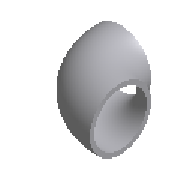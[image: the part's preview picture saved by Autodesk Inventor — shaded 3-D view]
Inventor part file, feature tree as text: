
AUTODESK INVENTOR PART (.ipt)
format: ipt  version: 2023.2 (Build 272271030, 271C)  size: 188,928 bytes
history: native  units: mm (DEFAULTED — no unit token found)
features: other x4, sketch x2, sweep x1
ambient origin geometry x8: Origin, YZ Plane, XZ Plane, XY Plane, X Axis, Y Axis, Z Axis, Center Point
bodies: Solid1 (feature_tree)
feature tree (7):
  sweep  "Sweep1"
  other  "Work Point1"
  other  "Work Point2"
  other  "Work Axis1"
  other  "Work Axis2"
  sketch  "Sketch1"  dims[d0=84.3mm d1=88.9mm]
  sketch  "Sketch2"  dims[d2=76.0mm d3=76.0mm d4=0.0mm d5=0.0mm]
